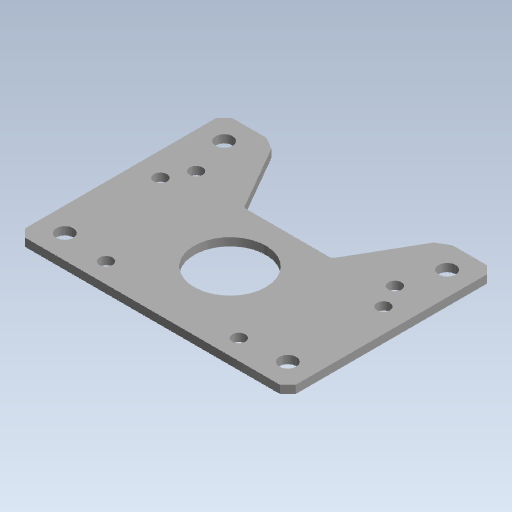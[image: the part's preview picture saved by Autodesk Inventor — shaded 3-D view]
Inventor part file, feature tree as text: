
AUTODESK INVENTOR PART (.ipt)
format: ipt  version: 2020 (Build 240168000, 168)  size: 84,480 bytes
history: native  units: mm (DEFAULTED — no unit token found)
features: fillet x1
ambient origin geometry x8: Origin, YZ Plane, XZ Plane, XY Plane, X Axis, Y Axis, Z Axis, Center Point
bodies: Solid1 (feature_tree)
feature tree (1):
  fillet  "Fillet1"  [1 undecoded]
note: 1 required parameter value undecoded (feature->parameter linkage not recoverable at this tier; creation-order binding heuristic only, values carry confidence <= 0.55)
